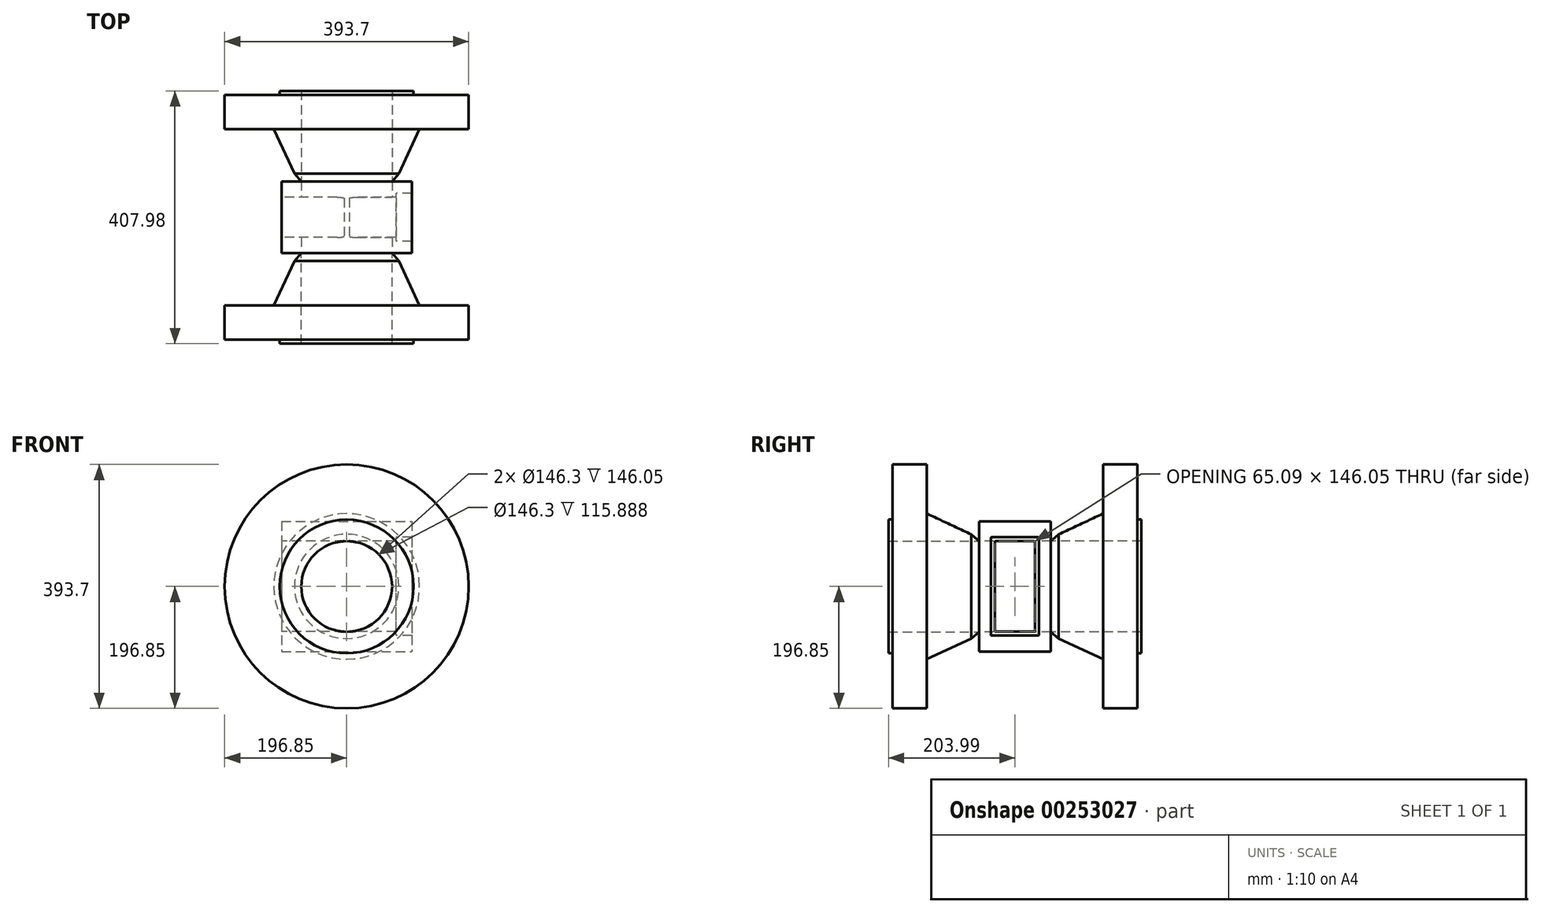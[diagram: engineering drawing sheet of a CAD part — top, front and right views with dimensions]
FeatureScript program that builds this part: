
annotation { "Feature Type Name" : "Feature", "Feature Type Description" : "" }
export const myFeature = defineFeature(function(context is Context, id is Id, definition is map)
    precondition{}
    {
        {
            var Q0;
            Q0=qCreatedBy(makeId("Front.planeOp"),FACE);
            var sketch = newSketch(context, id + "F0", { "sketchPlane" : qUnion([Q0])});
            skCircle(sketch, "E0", {"center": v(0, 0) * mm, "radius": 152.4 * mm});
            skLineSegment(sketch, "E1.bottom", {"start": v(-73.03, -73.03) * mm, "end": v(73.03, -73.03) * mm, "construction": true});
            skLineSegment(sketch, "E1.top", {"start": v(-73.03, 73.03) * mm, "end": v(73.03, 73.03) * mm, "construction": true});
            skLineSegment(sketch, "E1.left", {"start": v(-73.03, -73.03) * mm, "end": v(-73.03, 73.03) * mm, "construction": true});
            skLineSegment(sketch, "E1.right", {"start": v(73.03, -73.03) * mm, "end": v(73.03, 73.03) * mm, "construction": true});
            skLineSegment(sketch, "E2.bottom", {"start": v(-107.76, -107.76) * mm, "end": v(107.76, -107.76) * mm, "construction": true});
            skLineSegment(sketch, "E2.top", {"start": v(-107.76, 107.76) * mm, "end": v(107.76, 107.76) * mm, "construction": true});
            skLineSegment(sketch, "E2.left", {"start": v(-107.76, -107.76) * mm, "end": v(-107.76, 107.76) * mm, "construction": true});
            skLineSegment(sketch, "E2.right", {"start": v(107.76, -107.76) * mm, "end": v(107.76, 107.76) * mm, "construction": true});
            skLineSegment(sketch, "E3", {"start": v(0, 0) * mm, "end": v(0, 152.4) * mm});
            skLineSegment(sketch, "E4", {"start": v(0, 0) * mm, "end": v(152.4, 0) * mm});
            skPoint(sketch, "E4.endSnap0", {"position": v(107.76, 0) * mm});
            skSolve(sketch);
        }
        {
            var Q0;
            Q0 = qSketchRegion(id + "F0", true);
            extrude(context, id + "F1", {"entities" : qUnion([Q0]), "endBound" : BoundingType.SYMMETRIC, "depth" : 115.89 * mm, "offsetDistance" : 25.4 * mm});
        }
        {
            var Q0;
            Q0=qCreatedBy(makeId("Right.planeOp"),FACE);
            var sketch = newSketch(context, id + "F2", { "sketchPlane" : qUnion([Q0])});
            skLineSegment(sketch, "E5.bottom", {"start": v(30.96, -73.03) * mm, "end": v(-30.96, -73.03) * mm});
            skLineSegment(sketch, "E5.top", {"start": v(30.96, 73.03) * mm, "end": v(-30.96, 73.03) * mm});
            skLineSegment(sketch, "E5.left", {"start": v(32.54, -71.44) * mm, "end": v(32.54, 71.44) * mm});
            skLineSegment(sketch, "E5.right", {"start": v(-32.54, -71.44) * mm, "end": v(-32.54, 71.44) * mm});
            skPoint(sketch, "E5.middle", {"position": v(0, 0) * mm});
            skLineSegment(sketch, "E6", {"start": v(-32.54, 0) * mm, "end": v(32.54, 0) * mm, "construction": true});
            skPoint(sketch, "E7.visualSharp", {"position": v(32.54, 73.03) * mm});
            skArc(sketch, "E7.filletArc", {"start": v(32.54, 71.44) * mm, "mid": v(32.08, 72.56) * mm, "end": v(30.96, 73.03) * mm});
            skPoint(sketch, "E8.visualSharp", {"position": v(32.54, -73.03) * mm});
            skArc(sketch, "E8.filletArc", {"start": v(30.96, -73.03) * mm, "mid": v(32.08, -72.56) * mm, "end": v(32.54, -71.44) * mm});
            skPoint(sketch, "E9.visualSharp", {"position": v(-32.54, -73.03) * mm});
            skArc(sketch, "E9.filletArc", {"start": v(-32.54, -71.44) * mm, "mid": v(-32.08, -72.56) * mm, "end": v(-30.96, -73.03) * mm});
            skPoint(sketch, "E10.visualSharp", {"position": v(-32.54, 73.03) * mm});
            skArc(sketch, "E10.filletArc", {"start": v(-30.96, 73.03) * mm, "mid": v(-32.08, 72.56) * mm, "end": v(-32.54, 71.44) * mm});
            skSolve(sketch);
        }
        {
            var Q0;
            Q0 = qSketchRegion(id + "F2", true);
            extrude(context, id + "F3", {"entities" : qUnion([Q0]), "operationType" : NewBodyOperationType.REMOVE, "endBound" : BoundingType.THROUGH_ALL, "depth" : 25.4 * mm, "offsetDistance" : 25.4 * mm, "hasSecondDirection" : true, "secondDirectionBound" : SecondDirectionBoundingType.THROUGH_ALL, "secondDirectionOppositeDirection" : true, "secondDirectionDepth" : 25.4 * mm});
        }
        {
            var Q0;
            Q0=qCreatedBy(makeId("Front.planeOp"),FACE);
            var sketch = newSketch(context, id + "F4", { "sketchPlane" : qUnion([Q0])});
            skCircle(sketch, "E11", {"center": v(0, 0) * mm, "radius": 73.15 * mm});
            skSolve(sketch);
        }
        {
            var Q0;
            Q0 = qSketchRegion(id + "F4", true);
            extrude(context, id + "F5", {"entities" : qUnion([Q0]), "operationType" : NewBodyOperationType.REMOVE, "endBound" : BoundingType.THROUGH_ALL, "oppositeDirection" : true, "depth" : 25.4 * mm, "offsetDistance" : 25.4 * mm, "hasSecondDirection" : true, "secondDirectionBound" : SecondDirectionBoundingType.THROUGH_ALL, "secondDirectionOppositeDirection" : false, "secondDirectionDepth" : 25.4 * mm});
        }
        {
            var Q0;
            Q0=qCreatedBy(makeId("Right.planeOp"),FACE);
            cPlane(context, id + "F6", {"entities" : qUnion([Q0]), "cplaneType" : CPlaneType.OFFSET, "offset" : 79.5 * mm, "width" : 152.4 * mm, "height" : 152.4 * mm});
        }
        {
            var Q0;
            Q0=qCreatedBy(id+"F6.planeOp",FACE);
            var sketch = newSketch(context, id + "F7", { "sketchPlane" : qUnion([Q0])});
            skLineSegment(sketch, "E12.bottom", {"start": v(-37.3, -79.38) * mm, "end": v(37.3, -79.38) * mm});
            skLineSegment(sketch, "E12.top", {"start": v(-37.3, 79.38) * mm, "end": v(37.3, 79.38) * mm});
            skLineSegment(sketch, "E12.left", {"start": v(-38.9, -77.79) * mm, "end": v(-38.9, 77.79) * mm});
            skLineSegment(sketch, "E12.right", {"start": v(38.9, -77.79) * mm, "end": v(38.9, 77.79) * mm});
            skPoint(sketch, "E12.middle", {"position": v(0, 0) * mm});
            skPoint(sketch, "E13.visualSharp", {"position": v(38.9, 79.38) * mm});
            skArc(sketch, "E13.filletArc", {"start": v(38.9, 77.79) * mm, "mid": v(38.43, 78.91) * mm, "end": v(37.3, 79.38) * mm});
            skPoint(sketch, "E14.visualSharp", {"position": v(-38.9, 79.38) * mm});
            skArc(sketch, "E14.filletArc", {"start": v(-37.3, 79.38) * mm, "mid": v(-38.43, 78.91) * mm, "end": v(-38.9, 77.79) * mm});
            skPoint(sketch, "E15.visualSharp", {"position": v(-38.9, -79.38) * mm});
            skArc(sketch, "E15.filletArc", {"start": v(-38.9, -77.79) * mm, "mid": v(-38.43, -78.91) * mm, "end": v(-37.3, -79.38) * mm});
            skPoint(sketch, "E16.visualSharp", {"position": v(38.9, -79.38) * mm});
            skArc(sketch, "E16.filletArc", {"start": v(37.3, -79.38) * mm, "mid": v(38.43, -78.91) * mm, "end": v(38.9, -77.79) * mm});
            skSolve(sketch);
        }
        {
            var Q0;
            Q0 = qSketchRegion(id + "F7", true);
            extrude(context, id + "F8", {"entities" : qUnion([Q0]), "operationType" : NewBodyOperationType.REMOVE, "endBound" : BoundingType.THROUGH_ALL, "depth" : 25.4 * mm, "offsetDistance" : 25.4 * mm});
        }
        {
            var Q0;
            Q0=qCreatedBy(makeId("Front.planeOp"),FACE);
            var sketch = newSketch(context, id + "F9", { "sketchPlane" : qUnion([Q0])});
            skLineSegment(sketch, "E17.bottom", {"start": v(-104.9, 104.9) * mm, "end": v(104.9, 104.9) * mm});
            skLineSegment(sketch, "E17.top", {"start": v(-104.9, -104.9) * mm, "end": v(104.9, -104.9) * mm});
            skLineSegment(sketch, "E17.left", {"start": v(-104.9, 104.9) * mm, "end": v(-104.9, -104.9) * mm});
            skLineSegment(sketch, "E17.right", {"start": v(104.9, 104.9) * mm, "end": v(104.9, -104.9) * mm});
            skPoint(sketch, "E17.middle", {"position": v(0, 0) * mm});
            skLineSegment(sketch, "E18.bottom", {"start": v(-152.4, 152.4) * mm, "end": v(152.4, 152.4) * mm});
            skLineSegment(sketch, "E18.top", {"start": v(-152.4, -152.4) * mm, "end": v(152.4, -152.4) * mm});
            skLineSegment(sketch, "E18.left", {"start": v(-152.4, 152.4) * mm, "end": v(-152.4, -152.4) * mm});
            skLineSegment(sketch, "E18.right", {"start": v(152.4, 152.4) * mm, "end": v(152.4, -152.4) * mm});
            skSolve(sketch);
        }
        {
            var Q0;
            Q0 = qSketchRegion(id + "F9", true);
            extrude(context, id + "F10", {"entities" : qUnion([Q0]), "operationType" : NewBodyOperationType.REMOVE, "endBound" : BoundingType.THROUGH_ALL, "oppositeDirection" : true, "depth" : 25.4 * mm, "offsetDistance" : 25.4 * mm, "hasSecondDirection" : true, "secondDirectionBound" : SecondDirectionBoundingType.THROUGH_ALL, "secondDirectionOppositeDirection" : false, "secondDirectionDepth" : 25.4 * mm});
        }
        {
            var Q0;
            Q0=qCreatedBy(makeId("Top.planeOp"),FACE);
            var sketch = newSketch(context, id + "F11", { "sketchPlane" : qUnion([Q0])});
            skLineSegment(sketch, "E19", {"start": v(73.15, -57.94) * mm, "end": v(73.15, -204) * mm});
            skLineSegment(sketch, "E20", {"start": v(196.85, -197.64) * mm, "end": v(196.85, -142.02) * mm});
            skLineSegment(sketch, "E21", {"start": v(196.85, -142.02) * mm, "end": v(117.48, -142.02) * mm});
            skLineSegment(sketch, "E22", {"start": v(117.48, -142.02) * mm, "end": v(84.2, -70.71) * mm});
            skLineSegment(sketch, "E23", {"start": v(84.2, -70.71) * mm, "end": v(73.15, -57.94) * mm});
            skLineSegment(sketch, "E24", {"start": v(0, 0) * mm, "end": v(0, -204) * mm, "construction": true});
            skLineSegment(sketch, "E25", {"start": v(73.15, -204) * mm, "end": v(107.95, -204) * mm});
            skLineSegment(sketch, "E26", {"start": v(107.95, -204) * mm, "end": v(107.95, -197.64) * mm});
            skLineSegment(sketch, "E27", {"start": v(107.95, -197.64) * mm, "end": v(196.85, -197.64) * mm});
            skSolve(sketch);
        }
        {
            var Q0;
            Q0 = qSketchRegion(id + "F11", true);
            var Q1;
            Q1=sQuery(id+"F11.wireOp",EDGE,"E24");
            revolve(context, id + "F12", {"entities" : qUnion([Q0]), "axis" : qUnion([Q1]), "revolveType" : RevolveType.FULL});
        }
        {
            var Q0;
            Q0=makeQuery(id+"F12.opRevolve","SWEPT_BODY",BODY,{"disambiguationData":[OSD([sQuery(id+"F11.wireOp",EDGE,"E19"),sQuery(id+"F11.wireOp",EDGE,"E20"),sQuery(id+"F11.wireOp",EDGE,"E21"),sQuery(id+"F11.wireOp",EDGE,"E22"),sQuery(id+"F11.wireOp",EDGE,"E23"),sQuery(id+"F11.wireOp",EDGE,"E25"),sQuery(id+"F11.wireOp",EDGE,"E26"),sQuery(id+"F11.wireOp",EDGE,"E27")])]});
            var Q1;
            Q1=qCreatedBy(makeId("Front.planeOp"),FACE);
            mirror(context, id + "F14", {"entities" : qUnion([Q0]), "mirrorPlane" : qUnion([Q1])});
        }
    });
